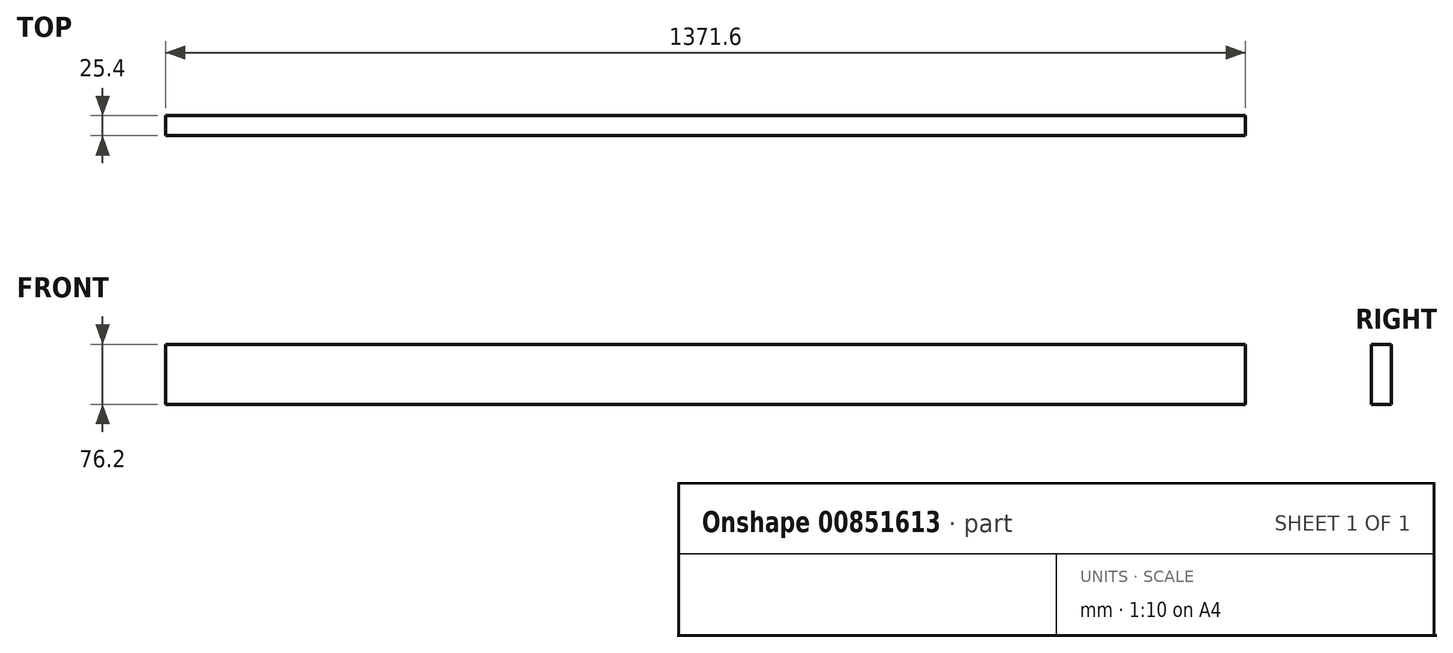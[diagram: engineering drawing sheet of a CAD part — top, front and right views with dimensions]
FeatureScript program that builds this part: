
annotation { "Feature Type Name" : "Feature", "Feature Type Description" : "" }
export const myFeature = defineFeature(function(context is Context, id is Id, definition is map)
    precondition{}
    {
        {
            var Q0;
            Q0=qCreatedBy(makeId("Front.planeOp"),FACE);
            var sketch = newSketch(context, id + "F0", { "sketchPlane" : qUnion([Q0])});
            skLineSegment(sketch, "E0", {"start": v(-327.26, -78.93) * mm, "end": v(-327.26, -155.13) * mm});
            skLineSegment(sketch, "E1", {"start": v(-327.26, -78.93) * mm, "end": v(1044.34, -78.93) * mm});
            skLineSegment(sketch, "E2", {"start": v(-327.26, -155.13) * mm, "end": v(1044.34, -155.13) * mm});
            skLineSegment(sketch, "E3", {"start": v(1044.34, -155.13) * mm, "end": v(1044.34, -78.93) * mm});
            skSolve(sketch);
        }
        {
            var Q0;
            Q0 = qSketchRegion(id + "F0", true);
            extrude(context, id + "F1", {"entities" : qUnion([Q0]), "depth" : 25.4 * mm, "offsetDistance" : 25.4 * mm});
        }
    });
